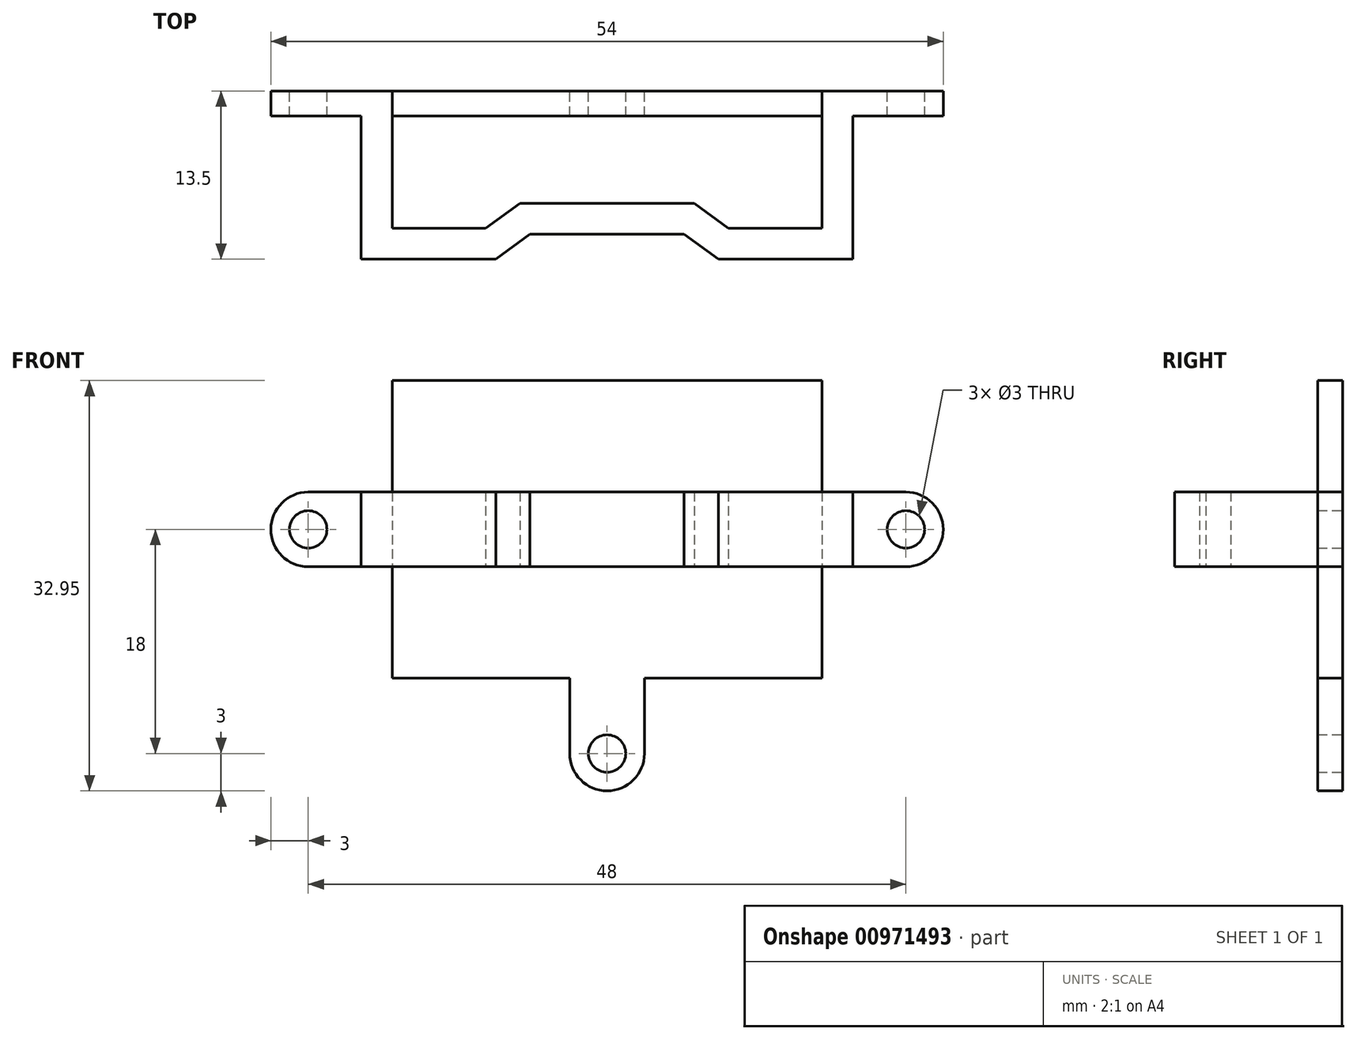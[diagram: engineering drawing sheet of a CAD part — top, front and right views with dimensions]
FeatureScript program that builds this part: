
annotation { "Feature Type Name" : "Feature", "Feature Type Description" : "" }
export const myFeature = defineFeature(function(context is Context, id is Id, definition is map)
    precondition{}
    {
        {
            var Q0;
            Q0=qCreatedBy(makeId("Front.planeOp"),FACE);
            var sketch = newSketch(context, id + "F0", { "sketchPlane" : qUnion([Q0])});
            skLineSegment(sketch, "E0.bottom", {"start": v(17.25, -11.95) * mm, "end": v(3, -11.95) * mm});
            skLineSegment(sketch, "E0.top", {"start": v(17.25, 11.95) * mm, "end": v(-17.25, 11.95) * mm});
            skLineSegment(sketch, "E0.left", {"start": v(17.25, -11.95) * mm, "end": v(17.25, -3) * mm});
            skLineSegment(sketch, "E0.right", {"start": v(-17.25, -11.95) * mm, "end": v(-17.25, -3) * mm});
            skPoint(sketch, "E0.middle", {"position": v(0, 0) * mm});
            skArc(sketch, "E1", {"start": v(-3, -18) * mm, "mid": v(0, -21) * mm, "end": v(3, -18) * mm});
            skArc(sketch, "E2", {"start": v(-24, 3) * mm, "mid": v(-27, 0) * mm, "end": v(-24, -3) * mm});
            skLineSegment(sketch, "E3", {"start": v(0, 7.47) * mm, "end": v(0, -5.14) * mm, "construction": true});
            skArc(sketch, "E4.MirrorC", {"start": v(24, 3) * mm, "mid": v(27, 0) * mm, "end": v(24, -3) * mm});
            skLineSegment(sketch, "E5", {"start": v(-3, -18) * mm, "end": v(-3, -11.95) * mm});
            skLineSegment(sketch, "E6.MirrorCS", {"start": v(3, -18) * mm, "end": v(3, -11.95) * mm});
            skLineSegment(sketch, "E7", {"start": v(-24, 3) * mm, "end": v(-17.25, 3) * mm});
            skLineSegment(sketch, "E8", {"start": v(-4.06, 0) * mm, "end": v(6.3, 0) * mm, "construction": true});
            skLineSegment(sketch, "E9.MirrorCS", {"start": v(-24, -3) * mm, "end": v(-17.25, -3) * mm});
            skLineSegment(sketch, "E10.MirrorCS", {"start": v(24, 3) * mm, "end": v(17.25, 3) * mm});
            skLineSegment(sketch, "E11.MirrorCS", {"start": v(24, -3) * mm, "end": v(17.25, -3) * mm});
            skLineSegment(sketch, "E12.trimOffspring", {"start": v(-17.25, 3) * mm, "end": v(-17.25, 11.95) * mm});
            skLineSegment(sketch, "E13.trimOffspring", {"start": v(-3, -11.95) * mm, "end": v(-17.25, -11.95) * mm});
            skLineSegment(sketch, "E14.trimOffspring", {"start": v(17.25, 3) * mm, "end": v(17.25, 11.95) * mm});
            skCircle(sketch, "E15", {"center": v(-24, 0) * mm, "radius": 1.5 * mm});
            skCircle(sketch, "E16.MirrorC", {"center": v(24, 0) * mm, "radius": 1.5 * mm});
            skCircle(sketch, "E17.MirrorC", {"center": v(0, -18) * mm, "radius": 1.5 * mm});
            skSolve(sketch);
        }
        {
            var Q0;
            Q0=qSketchRegion(id+"F0",true);
            extrude(context, id + "F1", {"entities" : qUnion([Q0]), "depth" : 2 * mm, "offsetDistance" : 25 * mm});
        }
        {
            var Q0;
            Q0=makeQuery(id+"F1.opExtrude","CAP_FACE",FACE,{"disambiguationData":[OSD([sQuery(id+"F0.wireOp",EDGE,"E0.bottom"),sQuery(id+"F0.wireOp",EDGE,"E0.top"),sQuery(id+"F0.wireOp",EDGE,"E0.left"),sQuery(id+"F0.wireOp",EDGE,"E0.right"),sQuery(id+"F0.wireOp",EDGE,"E1"),sQuery(id+"F0.wireOp",EDGE,"E2"),sQuery(id+"F0.wireOp",EDGE,"E4.MirrorC"),sQuery(id+"F0.wireOp",EDGE,"E5"),sQuery(id+"F0.wireOp",EDGE,"E6.MirrorCS"),sQuery(id+"F0.wireOp",EDGE,"E7"),sQuery(id+"F0.wireOp",EDGE,"E9.MirrorCS"),sQuery(id+"F0.wireOp",EDGE,"E10.MirrorCS"),sQuery(id+"F0.wireOp",EDGE,"E11.MirrorCS"),sQuery(id+"F0.wireOp",EDGE,"E12.trimOffspring"),sQuery(id+"F0.wireOp",EDGE,"E13.trimOffspring"),sQuery(id+"F0.wireOp",EDGE,"E14.trimOffspring"),sQuery(id+"F0.wireOp",EDGE,"E15"),sQuery(id+"F0.wireOp",EDGE,"E16.MirrorC"),sQuery(id+"F0.wireOp",EDGE,"E17.MirrorC")])],"isStart":false});
            var sketch = newSketch(context, id + "F2", { "sketchPlane" : qUnion([Q0])});
            skLineSegment(sketch, "E18.0.0", {"start": v(-17.25, 3) * mm, "end": v(-24, 3) * mm, "construction": true});
            skArc(sketch, "E18.0.1", {"start": v(-24, 3) * mm, "mid": v(-27, 0) * mm, "end": v(-24, -3) * mm, "construction": true});
            skLineSegment(sketch, "E18.0.2", {"start": v(-24, -3) * mm, "end": v(-17.25, -3) * mm, "construction": true});
            skLineSegment(sketch, "E18.0.3", {"start": v(-17.25, -3) * mm, "end": v(-17.25, -11.95) * mm, "construction": true});
            skLineSegment(sketch, "E18.0.4", {"start": v(-17.25, -11.95) * mm, "end": v(-3, -11.95) * mm, "construction": true});
            skLineSegment(sketch, "E18.0.5", {"start": v(-3, -11.95) * mm, "end": v(-3, -18) * mm, "construction": true});
            skArc(sketch, "E18.0.6", {"start": v(-3, -18) * mm, "mid": v(0, -21) * mm, "end": v(3, -18) * mm, "construction": true});
            skLineSegment(sketch, "E18.0.7", {"start": v(3, -18) * mm, "end": v(3, -11.95) * mm, "construction": true});
            skLineSegment(sketch, "E18.0.8", {"start": v(3, -11.95) * mm, "end": v(17.25, -11.95) * mm, "construction": true});
            skLineSegment(sketch, "E18.0.9", {"start": v(17.25, -11.95) * mm, "end": v(17.25, -3) * mm, "construction": true});
            skLineSegment(sketch, "E18.0.10", {"start": v(17.25, -3) * mm, "end": v(24, -3) * mm, "construction": true});
            skArc(sketch, "E18.0.11", {"start": v(24, -3) * mm, "mid": v(27, 0) * mm, "end": v(24, 3) * mm, "construction": true});
            skLineSegment(sketch, "E18.0.12", {"start": v(24, 3) * mm, "end": v(17.25, 3) * mm, "construction": true});
            skLineSegment(sketch, "E18.0.13", {"start": v(17.25, 3) * mm, "end": v(17.25, 11.95) * mm, "construction": true});
            skLineSegment(sketch, "E18.0.14", {"start": v(17.25, 11.95) * mm, "end": v(-17.25, 11.95) * mm, "construction": true});
            skLineSegment(sketch, "E18.0.15", {"start": v(-17.25, 11.95) * mm, "end": v(-17.25, 3) * mm, "construction": true});
            skLineSegment(sketch, "E19.bottom", {"start": v(-17.25, 3) * mm, "end": v(-19.75, 3) * mm});
            skLineSegment(sketch, "E19.top", {"start": v(-17.25, -3) * mm, "end": v(-19.75, -3) * mm});
            skLineSegment(sketch, "E19.left", {"start": v(-17.25, 3) * mm, "end": v(-17.25, -3) * mm});
            skLineSegment(sketch, "E19.right", {"start": v(-19.75, 3) * mm, "end": v(-19.75, -3) * mm});
            skLineSegment(sketch, "E20", {"start": v(0, 6.37) * mm, "end": v(0, -7.57) * mm, "construction": true});
            skLineSegment(sketch, "E21", {"start": v(-6.68, 0) * mm, "end": v(8.1, 0) * mm, "construction": true});
            skLineSegment(sketch, "E22.MirrorCS", {"start": v(17.25, 3) * mm, "end": v(19.75, 3) * mm});
            skLineSegment(sketch, "E23.MirrorCS", {"start": v(17.25, -3) * mm, "end": v(19.75, -3) * mm});
            skLineSegment(sketch, "E24.MirrorCS", {"start": v(17.25, 3) * mm, "end": v(17.25, -3) * mm});
            skLineSegment(sketch, "E25.MirrorCS", {"start": v(19.75, 3) * mm, "end": v(19.75, -3) * mm});
            skSolve(sketch);
        }
        {
            var Q0;
            Q0=qSketchRegion(id+"F2",true);
            extrude(context, id + "F3", {"entities" : qUnion([Q0]), "operationType" : NewBodyOperationType.ADD, "depth" : 9 * mm, "offsetDistance" : 25 * mm});
        }
        {
            var Q0;
            Q0=qCreatedBy(makeId("Top.planeOp"),FACE);
            var sketch = newSketch(context, id + "F4", { "sketchPlane" : qUnion([Q0])});
            skLineSegment(sketch, "E26.0.0", {"start": v(-24, 0) * mm, "end": v(-17.25, 0) * mm, "construction": true});
            skLineSegment(sketch, "E26.0.1", {"start": v(-17.25, 0) * mm, "end": v(-17.25, -2) * mm, "construction": true});
            skLineSegment(sketch, "E26.0.2", {"start": v(-17.25, -2) * mm, "end": v(-17.25, -11) * mm, "construction": true});
            skLineSegment(sketch, "E26.0.3", {"start": v(-17.25, -11) * mm, "end": v(-19.75, -11) * mm, "construction": true});
            skLineSegment(sketch, "E26.0.4", {"start": v(-19.75, -11) * mm, "end": v(-19.75, -2) * mm, "construction": true});
            skLineSegment(sketch, "E26.0.5", {"start": v(-19.75, -2) * mm, "end": v(-24, -2) * mm, "construction": true});
            skLineSegment(sketch, "E26.0.6", {"start": v(-24, -2) * mm, "end": v(-24, 0) * mm, "construction": true});
            skLineSegment(sketch, "E27.0.0", {"start": v(17.25, 0) * mm, "end": v(24, 0) * mm, "construction": true});
            skLineSegment(sketch, "E27.0.1", {"start": v(24, 0) * mm, "end": v(24, -2) * mm, "construction": true});
            skLineSegment(sketch, "E27.0.2", {"start": v(24, -2) * mm, "end": v(19.75, -2) * mm, "construction": true});
            skLineSegment(sketch, "E27.0.3", {"start": v(19.75, -2) * mm, "end": v(19.75, -11) * mm, "construction": true});
            skLineSegment(sketch, "E27.0.4", {"start": v(19.75, -11) * mm, "end": v(17.25, -11) * mm, "construction": true});
            skLineSegment(sketch, "E27.0.5", {"start": v(17.25, -11) * mm, "end": v(17.25, -2) * mm, "construction": true});
            skLineSegment(sketch, "E27.0.6", {"start": v(17.25, -2) * mm, "end": v(17.25, 0) * mm, "construction": true});
            skLineSegment(sketch, "E28", {"start": v(0, 2.97) * mm, "end": v(0, -5.47) * mm, "construction": true});
            skLineSegment(sketch, "E29", {"start": v(-19.75, -11) * mm, "end": v(-9.75, -11) * mm});
            skLineSegment(sketch, "E30", {"start": v(-9.75, -11) * mm, "end": v(-7, -9) * mm});
            skLineSegment(sketch, "E31", {"start": v(-7, -9) * mm, "end": v(0, -9) * mm});
            skLineSegment(sketch, "E32.0", {"start": v(-6.19, -11.5) * mm, "end": v(0, -11.5) * mm});
            skLineSegment(sketch, "E32.1", {"start": v(-8.94, -13.5) * mm, "end": v(-6.19, -11.5) * mm});
            skLineSegment(sketch, "E32.2", {"start": v(-19.75, -13.5) * mm, "end": v(-8.94, -13.5) * mm});
            skLineSegment(sketch, "E33", {"start": v(-19.75, -11) * mm, "end": v(-19.75, -13.5) * mm});
            skLineSegment(sketch, "E34.MirrorCS", {"start": v(19.75, -11) * mm, "end": v(19.75, -13.5) * mm});
            skLineSegment(sketch, "E35.MirrorCS", {"start": v(8.94, -13.5) * mm, "end": v(6.19, -11.5) * mm});
            skLineSegment(sketch, "E36.MirrorCS", {"start": v(17.25, -11) * mm, "end": v(19.75, -11) * mm, "construction": true});
            skLineSegment(sketch, "E37.MirrorCS", {"start": v(19.75, -13.5) * mm, "end": v(8.94, -13.5) * mm});
            skLineSegment(sketch, "E38.MirrorCS", {"start": v(7, -9) * mm, "end": v(0, -9) * mm});
            skLineSegment(sketch, "E39.MirrorCS", {"start": v(9.75, -11) * mm, "end": v(7, -9) * mm});
            skLineSegment(sketch, "E40.MirrorCS", {"start": v(19.75, -11) * mm, "end": v(9.75, -11) * mm});
            skLineSegment(sketch, "E41.MirrorCS", {"start": v(6.19, -11.5) * mm, "end": v(0, -11.5) * mm});
            skSolve(sketch);
        }
        {
            var Q0;
            Q0=qSketchRegion(id+"F4",true);
            extrude(context, id + "F5", {"entities" : qUnion([Q0]), "operationType" : NewBodyOperationType.ADD, "endBound" : BoundingType.SYMMETRIC, "depth" : 6 * mm, "offsetDistance" : 25 * mm});
        }
    });
